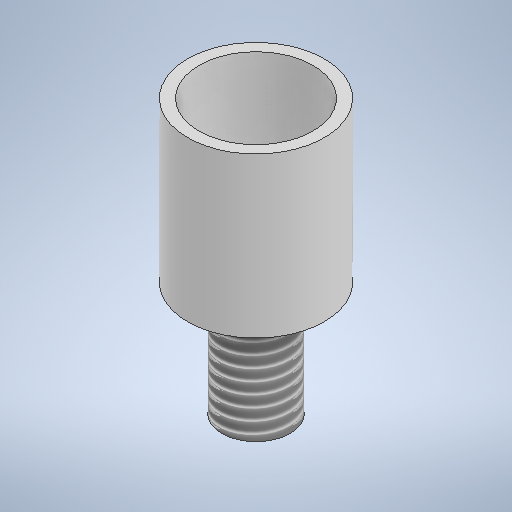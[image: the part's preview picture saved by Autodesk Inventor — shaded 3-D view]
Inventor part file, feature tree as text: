
AUTODESK INVENTOR PART (.ipt)
format: ipt  version: 2025.2 (Build 292293000, 293)  size: 249,344 bytes
history: native  units: mm
features: extrude x3, sketch x3, thread x1
ambient origin geometry x8: Origin, YZ Plane, XZ Plane, XY Plane, X Axis, Y Axis, Z Axis, Center Point
bodies: Solid1 (feature_tree)
feature tree (7):
  extrude  "Extrusion1"  Depth=5.0mm
  extrude  "Extrusion2"  Depth=6.0mm
  extrude  "Extrusion3"  Depth=3.0mm
  thread  "Thread2"  [1 undecoded]
  sketch  "Sketch1"  dims[d0=6.0mm d1=5.0mm]
  sketch  "Sketch2"  dims[d2=6.0mm d3=0.0mm d6=2.0mm]
  sketch  "Sketch3"  dims[d7=1.0mm d8=0.0mm d9=3.0mm d10=5.0mm d11=0.0mm d12=5.0mm d13=0.0mm]
note: 1 required parameter value undecoded (feature->parameter linkage not recoverable at this tier; creation-order binding heuristic only, values carry confidence <= 0.55)
